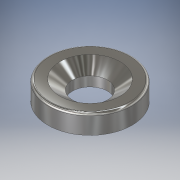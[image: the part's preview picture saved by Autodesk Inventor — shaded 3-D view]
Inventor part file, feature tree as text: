
AUTODESK INVENTOR PART (.ipt)
format: ipt  version: 2018 (Build 220112000, 112)  size: 129,024 bytes
history: native  units: in
note: dims shown in document units (in); Inventor stores cm internally (conversion verified against a paired STEP export)
features: revolve x1, fillet x1, sketch x1
ambient origin geometry x8: Origin, YZ Plane, XZ Plane, XY Plane, X Axis, Y Axis, Z Axis, Center Point
bodies: Solid1 (feature_tree)
feature tree (3):
  revolve  "Revolution1"  [1 undecoded]
  fillet  "Fillet1"  Radius=0.315in
  sketch  "Sketch1"  dims[d0=0.4035in d1=0.1575in d2=0.315in d3=0.1969in d4=90.0deg d5=0.0394in]
note: 1 required parameter value undecoded (feature->parameter linkage not recoverable at this tier; creation-order binding heuristic only, values carry confidence <= 0.55)
